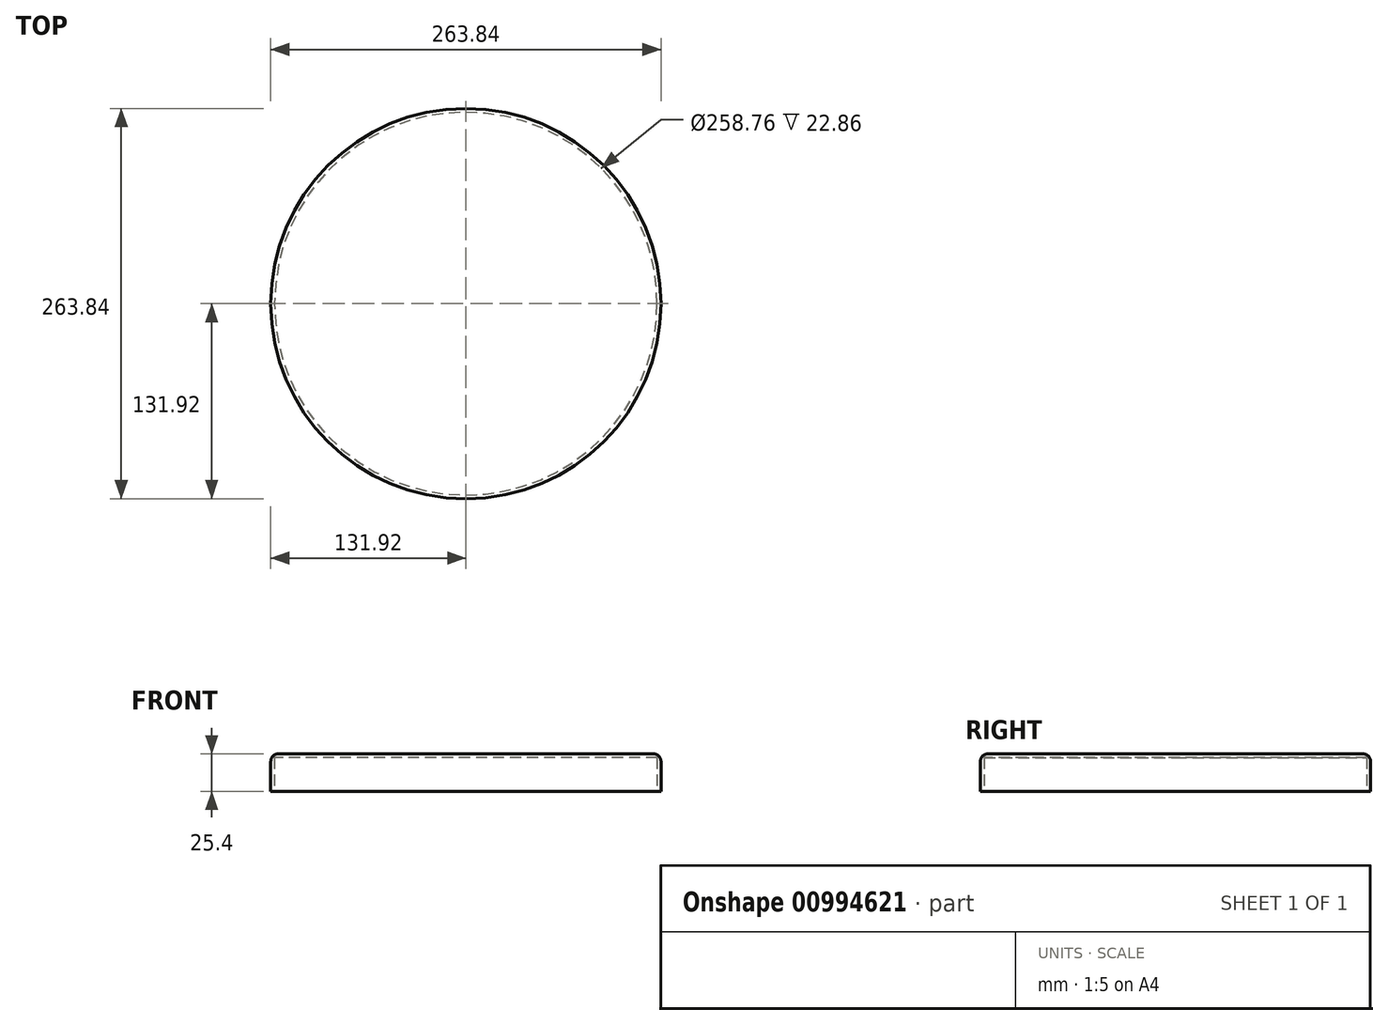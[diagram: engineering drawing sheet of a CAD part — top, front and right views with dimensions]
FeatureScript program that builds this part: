
annotation { "Feature Type Name" : "Feature", "Feature Type Description" : "" }
export const myFeature = defineFeature(function(context is Context, id is Id, definition is map)
    precondition{}
    {
        {
            var Q0;
            Q0=qCreatedBy(makeId("Top.planeOp"),FACE);
            var sketch = newSketch(context, id + "F0", { "sketchPlane" : qUnion([Q0])});
            skCircle(sketch, "E0", {"center": v(0, 0) * mm, "radius": 131.92 * mm});
            skSolve(sketch);
        }
        {
            var Q0;
            Q0=makeQuery(id+"F0.imprint","IMPRINT",FACE,{"disambiguationData":[TD([[makeQuery(id+"F0.imprint","IMPRINT",EDGE,{"derivedFrom":sQuery(id+"F0.wireOp",EDGE,"E0")}),1.0]])]});
            var Q1;
            Q1=sQuery(id+"F0.wireOp",EDGE,"E0");
            extrude(context, id + "F1", {"entities" : qUnion([Q0]), "surfaceEntities" : qUnion([Q1]), "depth" : 25.4 * mm, "offsetDistance" : 25.4 * mm});
        }
        {
            var Q0;
            Q0=makeQuery(id+"F1.opExtrude","CAP_FACE",FACE,{"disambiguationData":[OSD([sQuery(id+"F0.wireOp",EDGE,"E0")])],"isStart":true});
            shell(context, id + "F2", {"entities" : qUnion([Q0]), "thickness" : 2.54 * mm});
        }
        {
            var Q0;
            Q0=makeQuery(id+"F1.opExtrude","CAP_EDGE",EDGE,{"disambiguationData":[OSD([sQuery(id+"F0.wireOp",EDGE,"E0")])],"isStart":false});
            fillet(context, id + "F3", {"entities" : qUnion([Q0]), "radius" : 5.08 * mm, "tangentPropagation" : true, "allowEdgeOverflow" : false});
        }
    });
